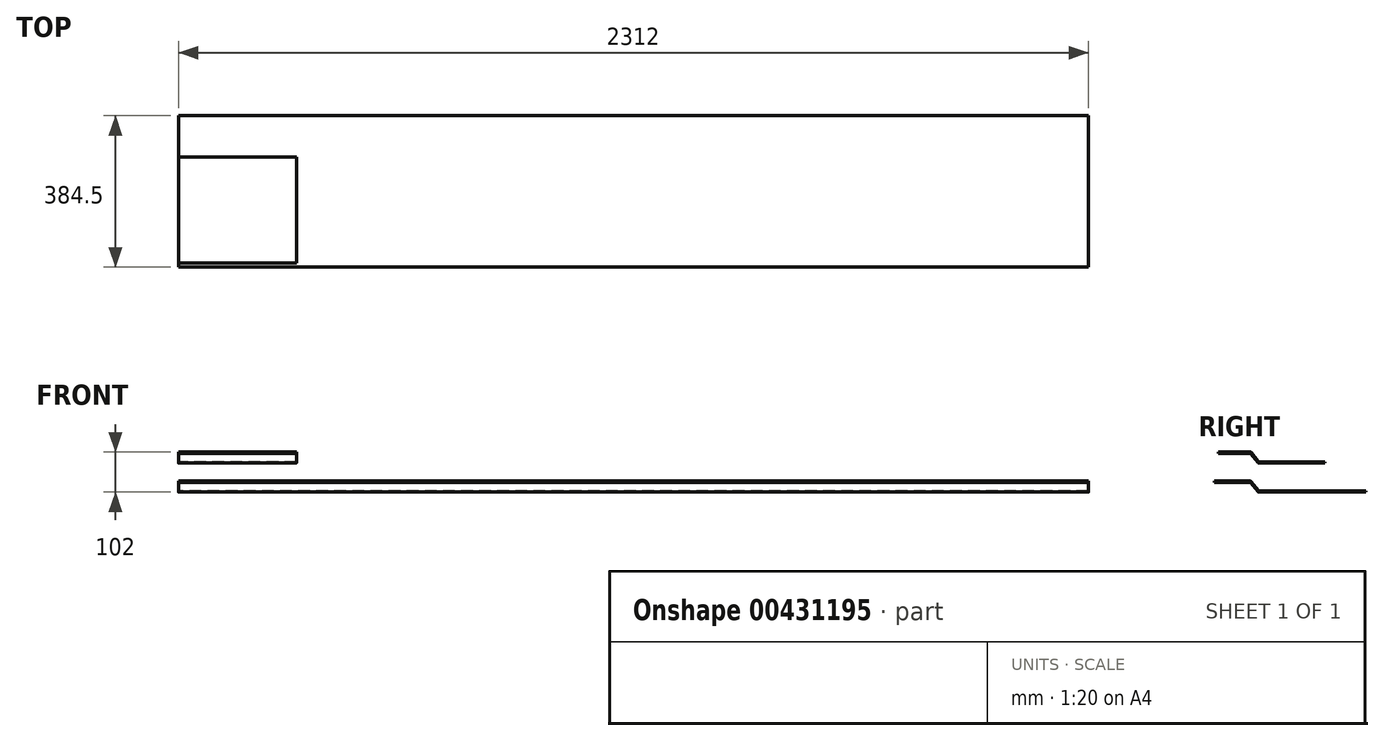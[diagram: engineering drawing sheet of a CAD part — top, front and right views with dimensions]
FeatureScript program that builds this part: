
annotation { "Feature Type Name" : "Feature", "Feature Type Description" : "" }
export const myFeature = defineFeature(function(context is Context, id is Id, definition is map)
    precondition{}
    {
        {
            var Q0;
            Q0=qCreatedBy(makeId("Right.planeOp"),FACE);
            var sketch = newSketch(context, id + "F0", { "sketchPlane" : qUnion([Q0])});
            skLineSegment(sketch, "E0", {"start": v(0, 0) * mm, "end": v(91.08, 0) * mm});
            skLineSegment(sketch, "E1", {"start": v(114.92, -25) * mm, "end": v(384.5, -25) * mm});
            skLineSegment(sketch, "E2", {"start": v(94.2, -1.5) * mm, "end": v(111.8, -23.5) * mm});
            skLineSegment(sketch, "E3.0", {"start": v(0, -3) * mm, "end": v(89.64, -3) * mm});
            skLineSegment(sketch, "E4.0", {"start": v(92.76, -4.5) * mm, "end": v(110.36, -26.5) * mm});
            skLineSegment(sketch, "E5.0", {"start": v(113.48, -28) * mm, "end": v(384.5, -28) * mm});
            skLineSegment(sketch, "E6", {"start": v(384.5, -28) * mm, "end": v(384.5, -25) * mm});
            skLineSegment(sketch, "E7", {"start": v(0, -3) * mm, "end": v(0, 0) * mm});
            skPoint(sketch, "E8.visualSharp", {"position": v(91.56, -3) * mm});
            skArc(sketch, "E8.filletArc", {"start": v(92.76, -4.5) * mm, "mid": v(91.37, -3.4) * mm, "end": v(89.64, -3) * mm});
            skPoint(sketch, "E9.visualSharp", {"position": v(93, 0) * mm});
            skArc(sketch, "E9.filletArc", {"start": v(94.2, -1.5) * mm, "mid": v(92.81, -0.4) * mm, "end": v(91.08, 0) * mm});
            skPoint(sketch, "E10.visualSharp", {"position": v(113, -25) * mm});
            skArc(sketch, "E10.filletArc", {"start": v(111.8, -23.5) * mm, "mid": v(113.19, -24.6) * mm, "end": v(114.92, -25) * mm});
            skPoint(sketch, "E11.visualSharp", {"position": v(111.56, -28) * mm});
            skArc(sketch, "E11.filletArc", {"start": v(110.36, -26.5) * mm, "mid": v(111.75, -27.6) * mm, "end": v(113.48, -28) * mm});
            skSolve(sketch);
        }
        {
            var Q0;
            Q0=makeQuery(id+"F0.imprint","IMPRINT",FACE,{"disambiguationData":[TD([[makeQuery(id+"F0.imprint","IMPRINT",EDGE,{"derivedFrom":sQuery(id+"F0.wireOp",EDGE,"E0")}),-1.0]])]});
            extrude(context, id + "F1", {"entities" : qUnion([Q0]), "depth" : 2312 * mm});
        }
        {
            var Q0;
            Q0=qCreatedBy(makeId("Right.planeOp"),FACE);
            var sketch = newSketch(context, id + "F2", { "sketchPlane" : qUnion([Q0])});
            skLineSegment(sketch, "E12", {"start": v(10, 74) * mm, "end": v(91.08, 74) * mm});
            skLineSegment(sketch, "E13", {"start": v(114.92, 49) * mm, "end": v(280, 49) * mm});
            skLineSegment(sketch, "E14", {"start": v(94.2, 72.5) * mm, "end": v(111.8, 50.5) * mm});
            skLineSegment(sketch, "E15.0", {"start": v(10, 71) * mm, "end": v(89.64, 71) * mm});
            skLineSegment(sketch, "E16.0", {"start": v(92.76, 69.5) * mm, "end": v(110.36, 47.5) * mm});
            skLineSegment(sketch, "E17.0", {"start": v(113.48, 46) * mm, "end": v(280, 46) * mm});
            skPoint(sketch, "E18.visualSharp", {"position": v(91.56, 71) * mm});
            skArc(sketch, "E18.filletArc", {"start": v(92.76, 69.5) * mm, "mid": v(91.37, 70.6) * mm, "end": v(89.64, 71) * mm});
            skPoint(sketch, "E19.visualSharp", {"position": v(93, 74) * mm});
            skArc(sketch, "E19.filletArc", {"start": v(94.2, 72.5) * mm, "mid": v(92.81, 73.6) * mm, "end": v(91.08, 74) * mm});
            skPoint(sketch, "E20.visualSharp", {"position": v(113, 49) * mm});
            skArc(sketch, "E20.filletArc", {"start": v(111.8, 50.5) * mm, "mid": v(113.19, 49.4) * mm, "end": v(114.92, 49) * mm});
            skPoint(sketch, "E21.visualSharp", {"position": v(111.56, 46) * mm});
            skArc(sketch, "E21.filletArc", {"start": v(110.36, 47.5) * mm, "mid": v(111.75, 46.4) * mm, "end": v(113.48, 46) * mm});
            skLineSegment(sketch, "E22", {"start": v(10, 74) * mm, "end": v(10, 71) * mm});
            skLineSegment(sketch, "E23", {"start": v(280, 46) * mm, "end": v(280, 49) * mm});
            skSolve(sketch);
        }
        {
            var Q0;
            Q0=makeQuery(id+"F2.imprint","IMPRINT",FACE,{"disambiguationData":[TD([[makeQuery(id+"F2.imprint","IMPRINT",EDGE,{"derivedFrom":sQuery(id+"F2.wireOp",EDGE,"E12")}),-1.0]])]});
            extrude(context, id + "F3", {"entities" : qUnion([Q0]), "depth" : 300 * mm});
        }
    });
